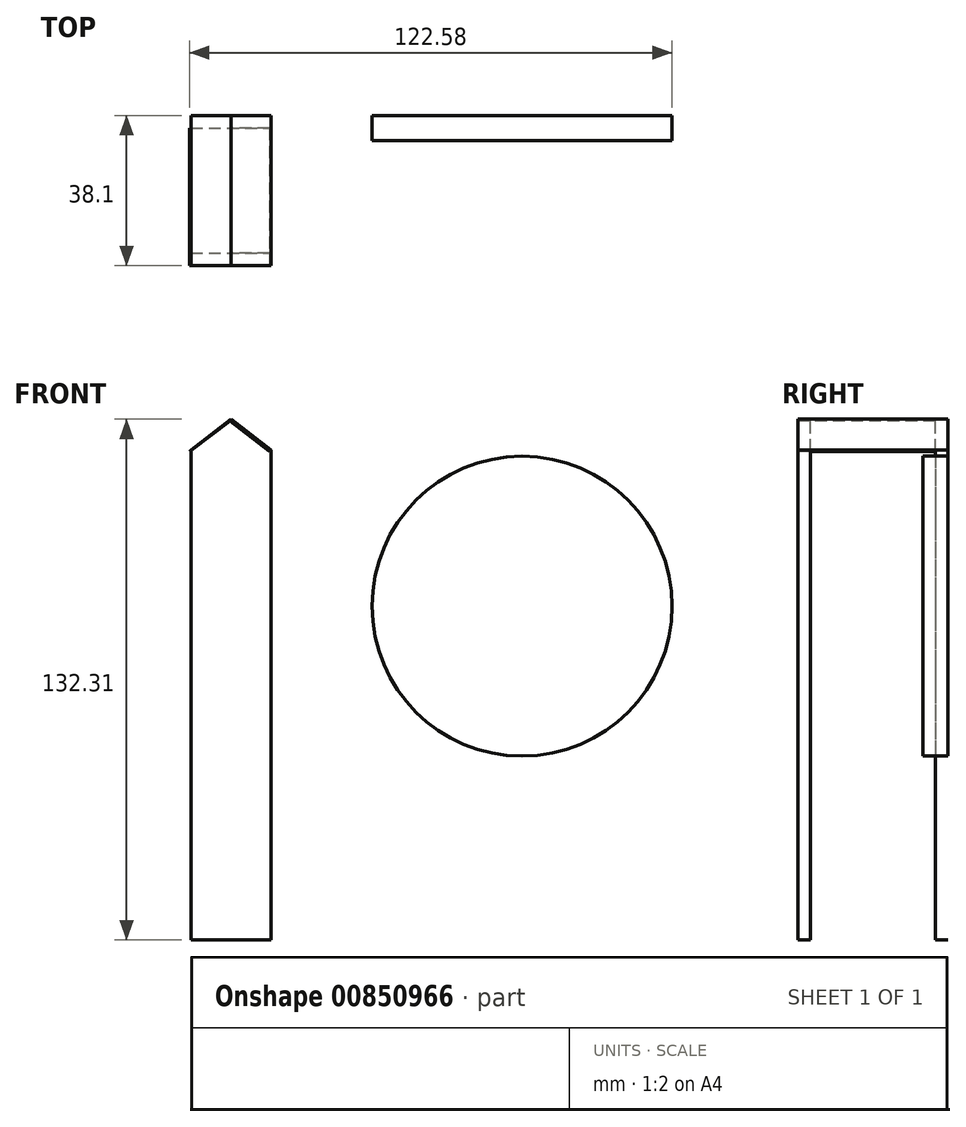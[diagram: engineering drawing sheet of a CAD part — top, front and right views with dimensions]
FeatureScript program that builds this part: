
annotation { "Feature Type Name" : "Feature", "Feature Type Description" : "" }
export const myFeature = defineFeature(function(context is Context, id is Id, definition is map)
    precondition{}
    {
        {
            var Q0;
            Q0=qCreatedBy(makeId("Front.planeOp"),FACE);
            var sketch = newSketch(context, id + "F0", { "sketchPlane" : qUnion([Q0])});
            skLineSegment(sketch, "E0.top", {"start": v(-10.28, -60.47) * mm, "end": v(10.04, -60.47) * mm});
            skLineSegment(sketch, "E0.left", {"start": v(-10.28, 63.99) * mm, "end": v(-10.28, -60.47) * mm});
            skLineSegment(sketch, "E0.right", {"start": v(10.04, 63.99) * mm, "end": v(10.04, -60.47) * mm});
            skPoint(sketch, "E1", {"position": v(0, 71.84) * mm});
            skLineSegment(sketch, "E2", {"start": v(10.04, 63.99) * mm, "end": v(0, 71.84) * mm});
            skLineSegment(sketch, "E3", {"start": v(-10.28, 63.99) * mm, "end": v(0, 71.84) * mm});
            skSolve(sketch);
        }
        {
            var Q0;
            Q0 = qSketchRegion(id + "F0", true);
            extrude(context, id + "F1", {"entities" : qUnion([Q0]), "depth" : 3.17 * mm, "offsetDistance" : 25.4 * mm});
        }
        {
            var Q0;
            Q0=makeQuery(id+"F1.opExtrude","SWEPT_FACE",FACE,{"disambiguationData":[OSD([sQuery(id+"F0.wireOp",EDGE,"E2")])]});
            var sketch = newSketch(context, id + "F2", { "sketchPlane" : qUnion([Q0])});
            skLineSegment(sketch, "E4.bottom", {"start": v(-31.48, 0) * mm, "end": v(-44.23, 0) * mm});
            skLineSegment(sketch, "E4.top", {"start": v(-31.48, -38.1) * mm, "end": v(-44.23, -38.1) * mm});
            skLineSegment(sketch, "E4.left", {"start": v(-31.48, 0) * mm, "end": v(-31.48, -38.1) * mm});
            skLineSegment(sketch, "E4.right", {"start": v(-44.23, 0) * mm, "end": v(-44.23, -38.1) * mm});
            skSolve(sketch);
        }
        {
            var Q0;
            Q0=makeQuery(id+"F1.opExtrude","SWEPT_FACE",FACE,{"disambiguationData":[OSD([sQuery(id+"F0.wireOp",EDGE,"E3")])]});
            var sketch = newSketch(context, id + "F3", { "sketchPlane" : qUnion([Q0])});
            skLineSegment(sketch, "E5.bottom", {"start": v(30.66, 0) * mm, "end": v(43.6, 0) * mm});
            skLineSegment(sketch, "E5.top", {"start": v(30.66, -38.1) * mm, "end": v(43.6, -38.1) * mm});
            skLineSegment(sketch, "E5.left", {"start": v(30.66, 0) * mm, "end": v(30.66, -38.1) * mm});
            skLineSegment(sketch, "E5.right", {"start": v(43.6, 0) * mm, "end": v(43.6, -38.1) * mm});
            skSolve(sketch);
        }
        {
            var Q0;
            {var subQ0=sQuery(id+"F2.wireOp",EDGE,"E4.top");Q0=makeQuery(id+"F2.imprint","IMPRINT",FACE,{"disambiguationData":[TD([[makeQuery(id+"F2.imprint","IMPRINT",EDGE,{"derivedFrom":subQ0}),-1.0]])]});}
            var Q1;
            {var subQ0=sQuery(id+"F3.wireOp",EDGE,"E5.top");Q1=makeQuery(id+"F3.imprint","IMPRINT",FACE,{"disambiguationData":[TD([[makeQuery(id+"F3.imprint","IMPRINT",EDGE,{"derivedFrom":subQ0}),1.0]])]});}
            extrude(context, id + "F4", {"entities" : qUnion([Q0, Q1]), "operationType" : NewBodyOperationType.ADD, "oppositeDirection" : true, "depth" : 0.56 * mm, "offsetDistance" : 25.4 * mm});
        }
        {
            var Q0;
            Q0=makeQuery(id+"F4.boolean.opBoolean","MERGE",FACE,{"derivedFrom":[makeQuery(id+"F4.opExtrude","SWEPT_FACE",FACE,{"disambiguationData":[OSD([sQuery(id+"F2.wireOp",EDGE,"E4.top")])]}),makeQuery(id+"F4.opExtrude","SWEPT_FACE",FACE,{"disambiguationData":[OSD([sQuery(id+"F3.wireOp",EDGE,"E5.top")])]})]});
            var sketch = newSketch(context, id + "F5", { "sketchPlane" : qUnion([Q0])});
            skLineSegment(sketch, "E6.bottom", {"start": v(-10.28, 63.99) * mm, "end": v(10.04, 63.99) * mm});
            skLineSegment(sketch, "E6.top", {"start": v(-10.28, -60.47) * mm, "end": v(10.04, -60.47) * mm});
            skLineSegment(sketch, "E6.left", {"start": v(-10.28, 63.99) * mm, "end": v(-10.28, -60.47) * mm});
            skLineSegment(sketch, "E6.right", {"start": v(10.04, 63.99) * mm, "end": v(10.04, -60.47) * mm});
            skSolve(sketch);
        }
        {
            var Q0;
            {var subQ1=sQuery(id+"F5.wireOp",EDGE,"E6.top");Q0=makeQuery(id+"F5.imprint","IMPRINT",FACE,{"disambiguationData":[TD([[makeQuery(id+"F5.imprint","IMPRINT",EDGE,{"derivedFrom":subQ1}),1.0]])]});}
            var Q1;
            {var subQ0=sQuery(id+"F5.wireOp",EDGE,"E6.bottom");var subQ1=makeQuery(id+"F4.opExtrude","CAP_EDGE",EDGE,{"disambiguationData":[OSD([sQuery(id+"F3.wireOp",EDGE,"E5.top")]),OD(0.0)],"isStart":false});var subQ2=makeQuery(id+"F5.imprint","INTERSECT",VERTEX,{"derivedFrom":[subQ1,subQ0]});Q1=makeQuery(id+"F5.imprint","IMPRINT",FACE,{"disambiguationData":[TD([[makeQuery(id+"F5.imprint","IMPRINT",EDGE,{"disambiguationData":[TD([[subQ2,-1.0]])],"derivedFrom":subQ0}),1.0]])]});}
            extrude(context, id + "F6", {"entities" : qUnion([Q0, Q1]), "oppositeDirection" : true, "depth" : 3.17 * mm, "offsetDistance" : 25.4 * mm});
        }
        {
            var Q0;
            Q0=qCreatedBy(makeId("Front.planeOp"),FACE);
            var sketch = newSketch(context, id + "F7", { "sketchPlane" : qUnion([Q0])});
            skCircle(sketch, "E7", {"center": v(73.86, 24.3) * mm, "radius": 38.1 * mm});
            skLineSegment(sketch, "E8.1.0", {"start": v(-95.68, 47.38) * mm, "end": v(-93.04, 45.86) * mm});
            skLineSegment(sketch, "E8.1.1", {"start": v(-93.03, 48.91) * mm, "end": v(-95.68, 47.38) * mm});
            skLineSegment(sketch, "E8.2.0", {"start": v(6.8, -106.56) * mm, "end": v(6.8, -103.5) * mm});
            skLineSegment(sketch, "E8.2.1", {"start": v(4.16, -105.03) * mm, "end": v(6.8, -106.56) * mm});
            skPoint(sketch, "E8.center", {"position": v(0, 0) * mm});
            skSolve(sketch);
        }
        {
            var Q0;
            Q0=makeQuery(id+"F7.imprint","IMPRINT",FACE,{"disambiguationData":[TD([[makeQuery(id+"F7.imprint","IMPRINT",EDGE,{"derivedFrom":sQuery(id+"F7.wireOp",EDGE,"E7")}),1.0]])]});
            extrude(context, id + "F8", {"entities" : qUnion([Q0]), "depth" : 6.35 * mm, "offsetDistance" : 25.4 * mm});
        }
    });
